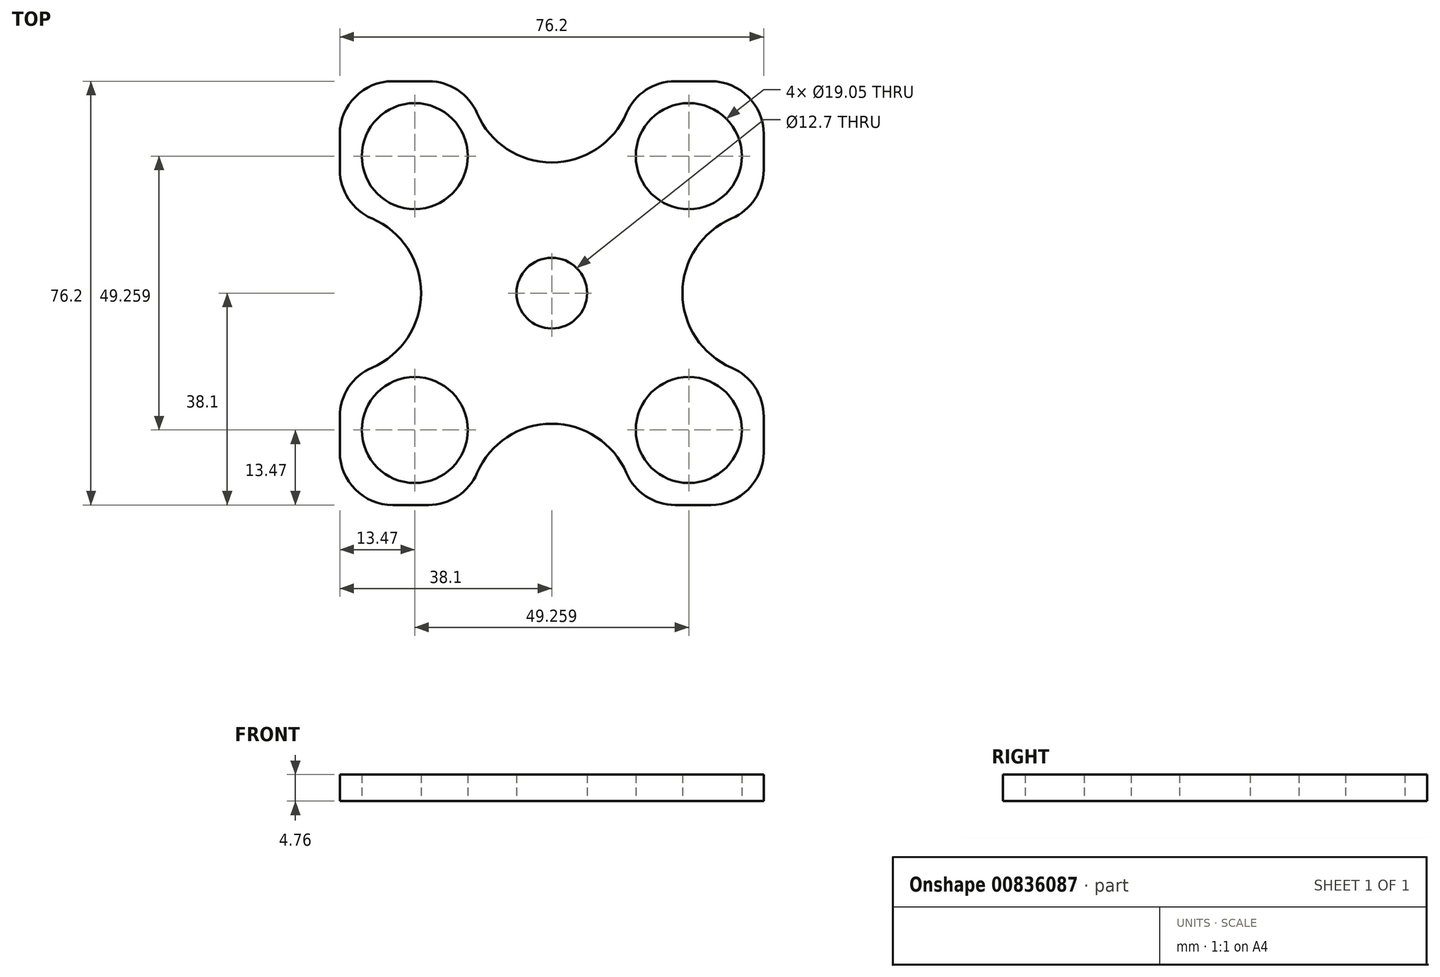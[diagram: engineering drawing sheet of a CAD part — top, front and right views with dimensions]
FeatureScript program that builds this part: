
annotation { "Feature Type Name" : "Feature", "Feature Type Description" : "" }
export const myFeature = defineFeature(function(context is Context, id is Id, definition is map)
    precondition{}
    {
        {
            var Q0;
            Q0=qCreatedBy(makeId("Top.planeOp"),FACE);
            var sketch = newSketch(context, id + "F0", { "sketchPlane" : qUnion([Q0])});
            skCircle(sketch, "E0", {"center": v(0, 0) * mm, "radius": 6.35 * mm});
            skLineSegment(sketch, "E1.bottom", {"start": v(-28.57, 38.1) * mm, "end": v(28.58, 38.1) * mm});
            skLineSegment(sketch, "E1.top", {"start": v(-28.58, -38.1) * mm, "end": v(28.57, -38.1) * mm});
            skLineSegment(sketch, "E1.left", {"start": v(-38.1, 28.58) * mm, "end": v(-38.1, -28.57) * mm});
            skLineSegment(sketch, "E1.right", {"start": v(38.1, 28.58) * mm, "end": v(38.1, -28.57) * mm});
            skLineSegment(sketch, "E2", {"start": v(0, 0) * mm, "end": v(-38.1, -38.1) * mm});
            skLineSegment(sketch, "E3", {"start": v(0, 0) * mm, "end": v(-38.1, 38.1) * mm});
            skLineSegment(sketch, "E4", {"start": v(0, 0) * mm, "end": v(38.1, 38.1) * mm});
            skLineSegment(sketch, "E5", {"start": v(0, 0) * mm, "end": v(38.1, -38.1) * mm});
            skLineSegment(sketch, "E6", {"start": v(0, 0) * mm, "end": v(0, -38.1) * mm});
            skLineSegment(sketch, "E7", {"start": v(0, 0) * mm, "end": v(38.1, 0) * mm});
            skLineSegment(sketch, "E8", {"start": v(0, 0) * mm, "end": v(0, 38.1) * mm});
            skLineSegment(sketch, "E9", {"start": v(0, 0) * mm, "end": v(-38.1, 0) * mm});
            skCircle(sketch, "E10", {"center": v(-24.63, 24.63) * mm, "radius": 9.53 * mm});
            skCircle(sketch, "E11.MirrorC", {"center": v(24.63, 24.63) * mm, "radius": 9.53 * mm});
            skCircle(sketch, "E12.MirrorC", {"center": v(24.63, -24.63) * mm, "radius": 9.53 * mm});
            skCircle(sketch, "E13.MirrorC", {"center": v(-24.63, -24.63) * mm, "radius": 9.53 * mm});
            skPoint(sketch, "E14.visualSharp", {"position": v(-38.1, -38.1) * mm});
            skArc(sketch, "E14.filletArc", {"start": v(-38.1, -28.57) * mm, "mid": v(-35.31, -35.31) * mm, "end": v(-28.58, -38.1) * mm});
            skPoint(sketch, "E15.visualSharp", {"position": v(38.1, -38.1) * mm});
            skArc(sketch, "E15.filletArc", {"start": v(28.57, -38.1) * mm, "mid": v(35.31, -35.31) * mm, "end": v(38.1, -28.57) * mm});
            skPoint(sketch, "E16.visualSharp", {"position": v(38.1, 38.1) * mm});
            skArc(sketch, "E16.filletArc", {"start": v(38.1, 28.58) * mm, "mid": v(35.31, 35.31) * mm, "end": v(28.58, 38.1) * mm});
            skPoint(sketch, "E17.visualSharp", {"position": v(-38.1, 38.1) * mm});
            skArc(sketch, "E17.filletArc", {"start": v(-28.57, 38.1) * mm, "mid": v(-35.31, 35.31) * mm, "end": v(-38.1, 28.58) * mm});
            skCircle(sketch, "E18", {"center": v(-38.1, 0) * mm, "radius": 14.6 * mm});
            skCircle(sketch, "E19.MirrorC", {"center": v(38.1, 0) * mm, "radius": 14.6 * mm});
            skCircle(sketch, "E20", {"center": v(0, -38.1) * mm, "radius": 14.6 * mm});
            skCircle(sketch, "E21.MirrorC", {"center": v(0, 38.1) * mm, "radius": 14.6 * mm});
            skSolve(sketch);
        }
        {
            var Q0;
            {var subQ7=sQuery(id+"F0.wireOp",EDGE,"E0");var subQ12=sQuery(id+"F0.wireOp",EDGE,"E9");var subQ13=makeQuery(id+"F0.imprint","INTERSECT",VERTEX,{"derivedFrom":[subQ7,subQ12]});Q0=makeQuery(id+"F0.imprint","IMPRINT",FACE,{"disambiguationData":[TD([[makeQuery(id+"F0.imprint","IMPRINT",EDGE,{"disambiguationData":[TD([[subQ13,-1.0]])],"derivedFrom":subQ7}),-1.0]])]});}
            var Q1;
            {var subQ0=sQuery(id+"F0.wireOp",EDGE,"E3");var subQ1=sQuery(id+"F0.wireOp",EDGE,"E0");var subQ2=makeQuery(id+"F0.imprint","INTERSECT",VERTEX,{"derivedFrom":[subQ1,subQ0]});Q1=makeQuery(id+"F0.imprint","IMPRINT",FACE,{"disambiguationData":[TD([[makeQuery(id+"F0.imprint","IMPRINT",EDGE,{"disambiguationData":[TD([[subQ2,-1.0]])],"derivedFrom":subQ1}),-1.0]])]});}
            var Q2;
            {var subQ5=sQuery(id+"F0.wireOp",EDGE,"E0");var subQ12=sQuery(id+"F0.wireOp",EDGE,"E8");var subQ13=makeQuery(id+"F0.imprint","INTERSECT",VERTEX,{"derivedFrom":[subQ5,subQ12]});Q2=makeQuery(id+"F0.imprint","IMPRINT",FACE,{"disambiguationData":[TD([[makeQuery(id+"F0.imprint","IMPRINT",EDGE,{"disambiguationData":[TD([[subQ13,-1.0]])],"derivedFrom":subQ5}),-1.0]])]});}
            var Q3;
            {var subQ1=sQuery(id+"F0.wireOp",EDGE,"E4");var subQ5=sQuery(id+"F0.wireOp",EDGE,"E0");var subQ6=makeQuery(id+"F0.imprint","INTERSECT",VERTEX,{"derivedFrom":[subQ5,subQ1]});Q3=makeQuery(id+"F0.imprint","IMPRINT",FACE,{"disambiguationData":[TD([[makeQuery(id+"F0.imprint","IMPRINT",EDGE,{"disambiguationData":[TD([[subQ6,-1.0]])],"derivedFrom":subQ5}),-1.0]])]});}
            var Q4;
            {var subQ0=sQuery(id+"F0.wireOp",EDGE,"E4");var subQ1=sQuery(id+"F0.wireOp",EDGE,"E0");var subQ2=makeQuery(id+"F0.imprint","INTERSECT",VERTEX,{"derivedFrom":[subQ1,subQ0]});Q4=makeQuery(id+"F0.imprint","IMPRINT",FACE,{"disambiguationData":[TD([[makeQuery(id+"F0.imprint","IMPRINT",EDGE,{"disambiguationData":[TD([[subQ2,1.0]])],"derivedFrom":subQ1}),-1.0]])]});}
            var Q5;
            {var subQ10=sQuery(id+"F0.wireOp",EDGE,"E0");var subQ12=sQuery(id+"F0.wireOp",EDGE,"E7");var subQ13=makeQuery(id+"F0.imprint","INTERSECT",VERTEX,{"derivedFrom":[subQ10,subQ12]});Q5=makeQuery(id+"F0.imprint","IMPRINT",FACE,{"disambiguationData":[TD([[makeQuery(id+"F0.imprint","IMPRINT",EDGE,{"disambiguationData":[TD([[subQ13,1.0]])],"derivedFrom":subQ10}),-1.0]])]});}
            var Q6;
            {var subQ5=sQuery(id+"F0.wireOp",EDGE,"E6");var subQ6=sQuery(id+"F0.wireOp",EDGE,"E0");var subQ7=makeQuery(id+"F0.imprint","INTERSECT",VERTEX,{"derivedFrom":[subQ6,subQ5]});Q6=makeQuery(id+"F0.imprint","IMPRINT",FACE,{"disambiguationData":[TD([[makeQuery(id+"F0.imprint","IMPRINT",EDGE,{"disambiguationData":[TD([[subQ7,-1.0]])],"derivedFrom":subQ6}),-1.0]])]});}
            var Q7;
            {var subQ1=sQuery(id+"F0.wireOp",EDGE,"E2");var subQ5=sQuery(id+"F0.wireOp",EDGE,"E0");var subQ6=makeQuery(id+"F0.imprint","INTERSECT",VERTEX,{"derivedFrom":[subQ5,subQ1]});Q7=makeQuery(id+"F0.imprint","IMPRINT",FACE,{"disambiguationData":[TD([[makeQuery(id+"F0.imprint","IMPRINT",EDGE,{"disambiguationData":[TD([[subQ6,-1.0]])],"derivedFrom":subQ5}),-1.0]])]});}
            extrude(context, id + "F1", {"entities" : qUnion([Q0, Q1, Q2, Q3, Q4, Q5, Q6, Q7]), "depth" : 4.76 * mm, "offsetDistance" : 25.4 * mm});
        }
        {
            var Q0;
            {var subQ0=sQuery(id+"F0.wireOp",EDGE,"E18");var subQ1=sQuery(id+"F0.wireOp",EDGE,"E1.left");Q0=makeQuery(id+"F1.opExtrude","SWEPT_EDGE",EDGE,{"disambiguationData":[OSD([subQ1,subQ0]),TDD([makeQuery(id+"F0.imprint","INTERSECT",VERTEX,{"disambiguationData":[OD(0.0)],"derivedFrom":[subQ1,subQ0]})])]});}
            var Q1;
            {var subQ0=sQuery(id+"F0.wireOp",EDGE,"E18");var subQ1=sQuery(id+"F0.wireOp",EDGE,"E1.left");Q1=makeQuery(id+"F1.opExtrude","SWEPT_EDGE",EDGE,{"disambiguationData":[OSD([subQ1,subQ0]),TDD([makeQuery(id+"F0.imprint","INTERSECT",VERTEX,{"disambiguationData":[OD(1.0)],"derivedFrom":[subQ1,subQ0]})])]});}
            var Q2;
            {var subQ0=sQuery(id+"F0.wireOp",EDGE,"E20");var subQ1=sQuery(id+"F0.wireOp",EDGE,"E1.top");Q2=makeQuery(id+"F1.opExtrude","SWEPT_EDGE",EDGE,{"disambiguationData":[OSD([subQ1,subQ0]),TDD([makeQuery(id+"F0.imprint","INTERSECT",VERTEX,{"disambiguationData":[OD(0.0)],"derivedFrom":[subQ1,subQ0]})])]});}
            var Q3;
            {var subQ0=sQuery(id+"F0.wireOp",EDGE,"E20");var subQ1=sQuery(id+"F0.wireOp",EDGE,"E1.top");Q3=makeQuery(id+"F1.opExtrude","SWEPT_EDGE",EDGE,{"disambiguationData":[OSD([subQ1,subQ0]),TDD([makeQuery(id+"F0.imprint","INTERSECT",VERTEX,{"disambiguationData":[OD(1.0)],"derivedFrom":[subQ1,subQ0]})])]});}
            var Q4;
            {var subQ0=sQuery(id+"F0.wireOp",EDGE,"E19.MirrorC");var subQ1=sQuery(id+"F0.wireOp",EDGE,"E1.right");Q4=makeQuery(id+"F1.opExtrude","SWEPT_EDGE",EDGE,{"disambiguationData":[OSD([subQ1,subQ0]),TDD([makeQuery(id+"F0.imprint","INTERSECT",VERTEX,{"disambiguationData":[OD(1.0)],"derivedFrom":[subQ1,subQ0]})])]});}
            var Q5;
            {var subQ0=sQuery(id+"F0.wireOp",EDGE,"E19.MirrorC");var subQ1=sQuery(id+"F0.wireOp",EDGE,"E1.right");Q5=makeQuery(id+"F1.opExtrude","SWEPT_EDGE",EDGE,{"disambiguationData":[OSD([subQ1,subQ0]),TDD([makeQuery(id+"F0.imprint","INTERSECT",VERTEX,{"disambiguationData":[OD(0.0)],"derivedFrom":[subQ1,subQ0]})])]});}
            var Q6;
            {var subQ0=sQuery(id+"F0.wireOp",EDGE,"E21.MirrorC");var subQ1=sQuery(id+"F0.wireOp",EDGE,"E1.bottom");Q6=makeQuery(id+"F1.opExtrude","SWEPT_EDGE",EDGE,{"disambiguationData":[OSD([subQ1,subQ0]),TDD([makeQuery(id+"F0.imprint","INTERSECT",VERTEX,{"disambiguationData":[OD(0.0)],"derivedFrom":[subQ1,subQ0]})])]});}
            var Q7;
            {var subQ0=sQuery(id+"F0.wireOp",EDGE,"E21.MirrorC");var subQ1=sQuery(id+"F0.wireOp",EDGE,"E1.bottom");Q7=makeQuery(id+"F1.opExtrude","SWEPT_EDGE",EDGE,{"disambiguationData":[OSD([subQ1,subQ0]),TDD([makeQuery(id+"F0.imprint","INTERSECT",VERTEX,{"disambiguationData":[OD(1.0)],"derivedFrom":[subQ1,subQ0]})])]});}
            fillet(context, id + "F2", {"entities" : qUnion([Q0, Q1, Q2, Q3, Q4, Q5, Q6, Q7]), "radius" : 9.52 * mm, "tangentPropagation" : true, "allowEdgeOverflow" : false});
        }
    });
